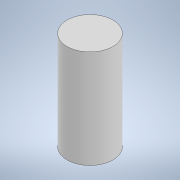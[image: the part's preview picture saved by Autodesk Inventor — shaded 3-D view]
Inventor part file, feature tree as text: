
AUTODESK INVENTOR PART (.ipt)
format: ipt  version: 2021 (Build 250183000, 183)  size: 89,600 bytes
history: native  units: in
note: dims shown in document units (in); Inventor stores cm internally (conversion verified against a paired STEP export)
features: extrude x1, sketch x1
ambient origin geometry x8: Origin, YZ Plane, XZ Plane, XY Plane, X Axis, Y Axis, Z Axis, Center Point
bodies: Solid1 (feature_tree)
feature tree (2):
  extrude  "Extrusion1"  Depth=0.375in TaperAngle=0.0deg
  sketch  "Sketch1"  dims[d0=0.175in d1=0.375in d2=0.0in]
